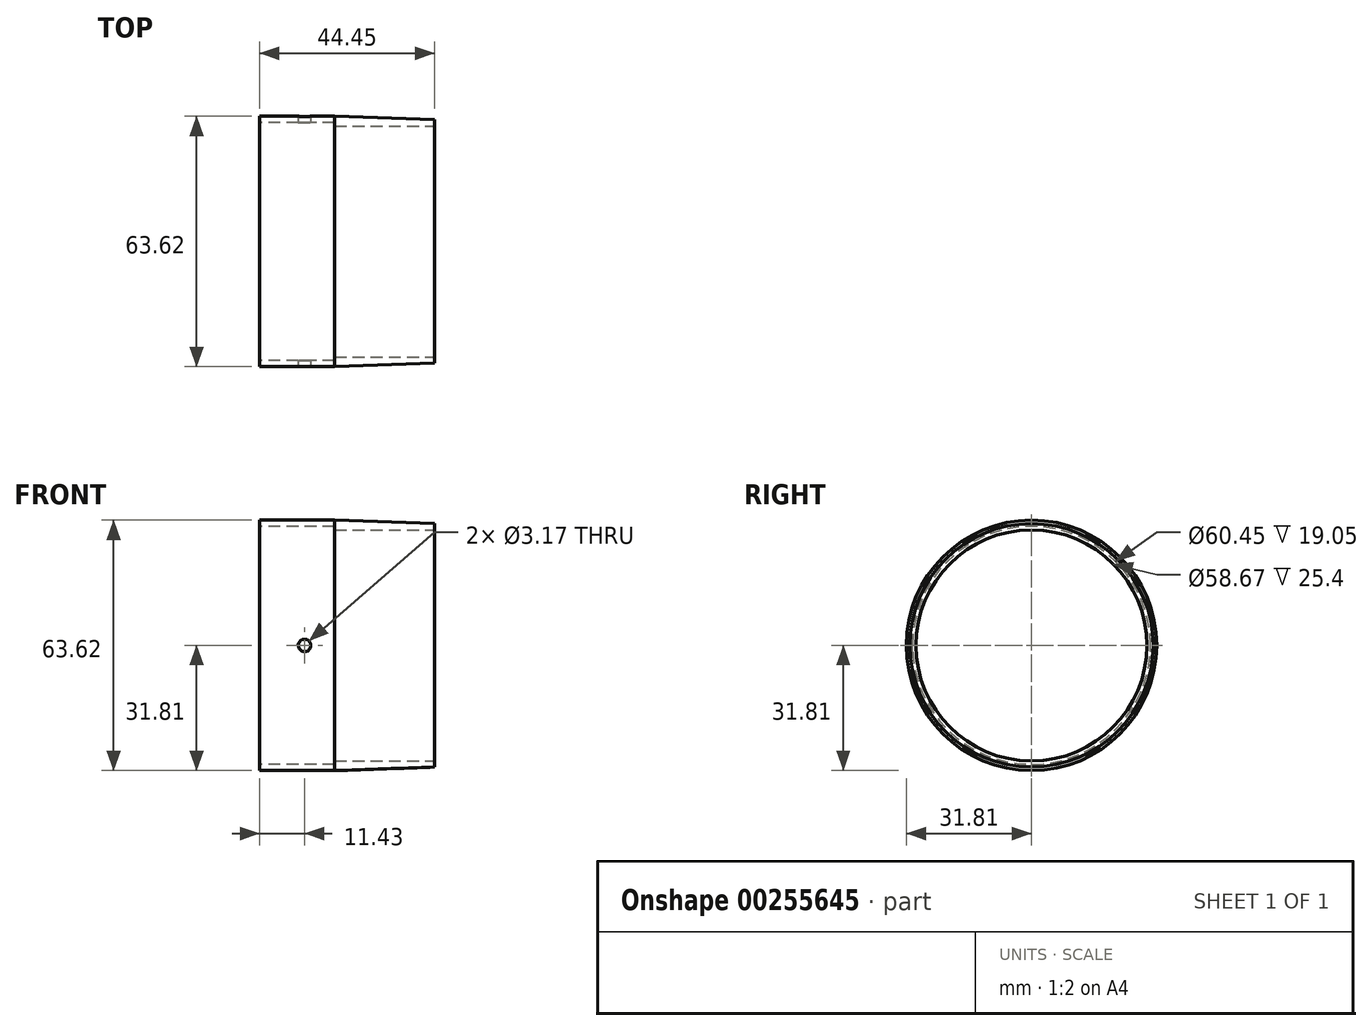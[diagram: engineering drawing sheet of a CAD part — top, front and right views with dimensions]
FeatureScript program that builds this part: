
annotation { "Feature Type Name" : "Feature", "Feature Type Description" : "" }
export const myFeature = defineFeature(function(context is Context, id is Id, definition is map)
    precondition{}
    {
        {
            var Q0;
            Q0=qCreatedBy(makeId("Right.planeOp"),FACE);
            var sketch = newSketch(context, id + "F0", { "sketchPlane" : qUnion([Q0])});
            skCircle(sketch, "E0", {"center": v(0, 0) * mm, "radius": 31.81 * mm});
            skSolve(sketch);
        }
        {
            var Q0;
            Q0 = qSketchRegion(id + "F0", true);
            extrude(context, id + "F1", {"entities" : qUnion([Q0]), "depth" : 19.05 * mm});
        }
        {
            var Q0;
            Q0=makeQuery(id+"F1.opExtrude","CAP_FACE",FACE,{"disambiguationData":[OSD([sQuery(id+"F0.wireOp",EDGE,"E0")])],"isStart":false});
            cPlane(context, id + "F2", {"entities" : qUnion([Q0]), "cplaneType" : CPlaneType.OFFSET, "offset" : 25.4 * mm, "width" : 152.4 * mm, "height" : 152.4 * mm});
        }
        {
            var Q0;
            Q0=qCreatedBy(id+"F2.planeOp",FACE);
            var sketch = newSketch(context, id + "F3", { "sketchPlane" : qUnion([Q0])});
            skPoint(sketch, "E1.0", {"position": v(0, 0) * mm});
            skCircle(sketch, "E2", {"center": v(0, 0) * mm, "radius": 30.92 * mm});
            skSolve(sketch);
        }
        {
            var Q1;
            Q1=makeQuery(id+"F1.opExtrude","CAP_FACE",FACE,{"disambiguationData":[OSD([sQuery(id+"F0.wireOp",EDGE,"E0")])],"isStart":false});
            var Q2;
            Q2=makeQuery(id+"F3.imprint","IMPRINT",FACE,{"disambiguationData":[TD([[makeQuery(id+"F3.imprint","IMPRINT",EDGE,{"derivedFrom":sQuery(id+"F3.wireOp",EDGE,"E2")}),1.0]])]});
            loft(context, id + "F4", {"operationType" : NewBodyOperationType.ADD, "sheetProfilesArray" : [{ "sheetProfileEntities" : qUnion([Q1]) }, { "sheetProfileEntities" : qUnion([Q2]) }]});
        }
        {
            var Q0;
            Q0=makeQuery(id+"F1.opExtrude","CAP_FACE",FACE,{"disambiguationData":[OSD([sQuery(id+"F0.wireOp",EDGE,"E0")])],"isStart":true});
            var sketch = newSketch(context, id + "F5", { "sketchPlane" : qUnion([Q0])});
            skCircle(sketch, "E3", {"center": v(0, 0) * mm, "radius": 30.23 * mm});
            skSolve(sketch);
        }
        {
            var Q0;
            Q0 = qSketchRegion(id + "F5", true);
            extrude(context, id + "F6", {"entities" : qUnion([Q0]), "operationType" : NewBodyOperationType.REMOVE, "oppositeDirection" : true, "depth" : 19.05 * mm});
        }
        {
            var Q0;
            Q0=makeQuery(id+"F4.opLoft","CAP_FACE",FACE,{"disambiguationData":[OSD([makeQuery(id+"F3.imprint","IMPRINT",FACE,{"disambiguationData":[TD([[makeQuery(id+"F3.imprint","IMPRINT",EDGE,{"derivedFrom":sQuery(id+"F3.wireOp",EDGE,"E2")}),1.0]])]})])],"isStart":true});
            var sketch = newSketch(context, id + "F7", { "sketchPlane" : qUnion([Q0])});
            skCircle(sketch, "E4", {"center": v(0, 0) * mm, "radius": 29.34 * mm});
            skSolve(sketch);
        }
        {
            var Q0;
            Q0=makeQuery(id+"F7.imprint","IMPRINT",FACE,{"disambiguationData":[TD([[makeQuery(id+"F7.imprint","IMPRINT",EDGE,{"derivedFrom":sQuery(id+"F7.wireOp",EDGE,"E4")}),1.0]])]});
            extrude(context, id + "F8", {"entities" : qUnion([Q0]), "operationType" : NewBodyOperationType.REMOVE, "endBound" : BoundingType.UP_TO_NEXT, "oppositeDirection" : true, "depth" : 25.4 * mm});
        }
        {
            var Q0;
            Q0=qCreatedBy(makeId("Front.planeOp"),FACE);
            var sketch = newSketch(context, id + "F9", { "sketchPlane" : qUnion([Q0])});
            skLineSegment(sketch, "E5", {"start": v(0, 31.81) * mm, "end": v(19.37, 31.81) * mm, "construction": true});
            skLineSegment(sketch, "E6", {"start": v(19.05, -31.81) * mm, "end": v(0, -31.81) * mm, "construction": true});
            skLineSegment(sketch, "E7", {"start": v(11.43, 31.81) * mm, "end": v(11.43, -31.81) * mm, "construction": true});
            skCircle(sketch, "E8", {"center": v(11.43, 0) * mm, "radius": 1.59 * mm});
            skSolve(sketch);
        }
        {
            var Q0;
            Q0 = qSketchRegion(id + "F9", true);
            extrude(context, id + "F10", {"entities" : qUnion([Q0]), "operationType" : NewBodyOperationType.REMOVE, "endBound" : BoundingType.THROUGH_ALL, "oppositeDirection" : true, "depth" : 25.4 * mm, "hasSecondDirection" : true, "secondDirectionBound" : SecondDirectionBoundingType.THROUGH_ALL, "secondDirectionOppositeDirection" : false, "secondDirectionDepth" : 25.4 * mm});
        }
    });
